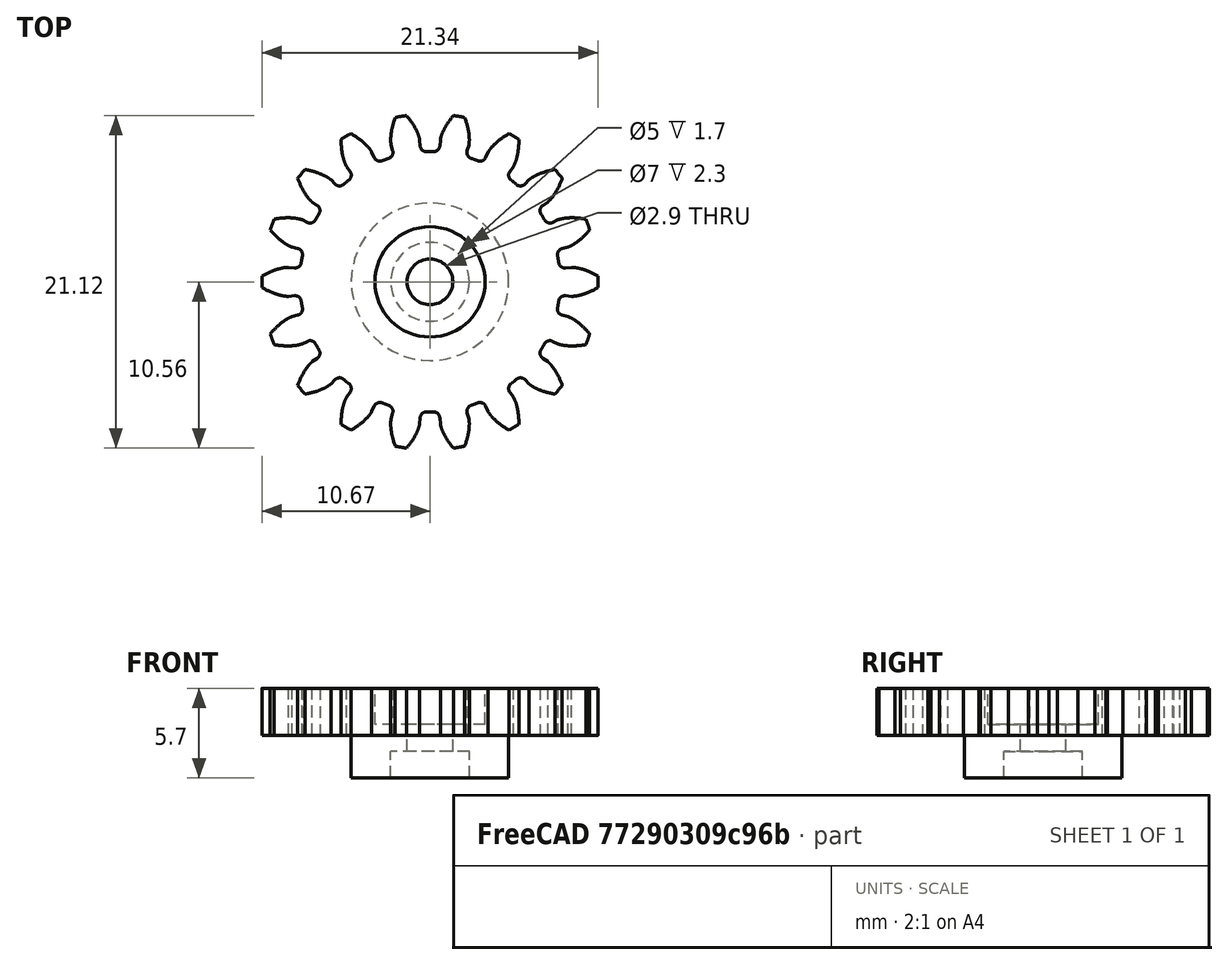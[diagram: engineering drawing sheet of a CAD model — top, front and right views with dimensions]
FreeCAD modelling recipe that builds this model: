
FCSTD DOCUMENT  (FreeCAD 0.17R13541 (Git))
Label: gear 18 low (new)
License: All rights reserved
LicenseURL: http://en.wikipedia.org/wiki/All_rights_reserved
objects: Part::Cylinder×5, Part::Cut×4, Part::Part2DObjectPython×1, Part::Extrusion×1, Part::MultiFuse×1
note: 12 computed .brp shape members not serialized (recipe doc carries the construction recipe); baked Part::Feature solids carry a one-line shape summary decoded from their .brp

FEATURE [Part::Part2DObjectPython] InvoluteGear  label="Engranaje 1 raw"  # Draft 2D object (typed FeaturePython)
  ExternalGear = true
  HighPrecision = true
  Modules = 1.0667
  NumberOfTeeth = 18
  PressureAngle = 20
  expr: Modules = 1.0667
FEATURE [Part::Extrusion] Extrude  label="Engranaje 1"
  Base = -> InvoluteGear
  Dir = (0,0,1)
  DirMode = 2
  FaceMakerClass = Part::FaceMakerBullseye
  LengthFwd = 3
  LengthRev = 0
  Solid = true
  Symmetric = false
FEATURE [Part::Cylinder] Cylinder  label="Cilindro"
  Angle = 360
  AttacherType = Attacher::AttachEngine3D
  Height = 10
  Placement = pos=(0,0,-2) rot=(0,0,1;0rad)
  Radius = 1.45
FEATURE [Part::Cut] Cut  label="Engranaje 1 agujereado"
  Base = -> Extrude
  Refine = true
  Tool = -> Cylinder
FEATURE [Part::Cylinder] Cylinder001  label="Cilindro exterior"
  Angle = 360
  AttacherType = Attacher::AttachEngine3D
  Height = 2.7
  Placement = pos=(0,0,-2.7) rot=(0,0,1;0rad)
  Radius = 5
FEATURE [Part::Cylinder] Cylinder002  label="Cilindro interior"
  Angle = 360
  AttacherType = Attacher::AttachEngine3D
  Height = 2.7
  Placement = pos=(0,0,-3.7) rot=(0,0,1;0rad)
  Radius = 2.5
FEATURE [Part::Cut] Cut001  label="Cilindro inferior"
  Base = -> Cylinder001
  Refine = true
  Tool = -> Cylinder002
FEATURE [Part::Cylinder] Cylinder003  label="Cilindro superior"
  Angle = 360
  AttacherType = Attacher::AttachEngine3D
  Height = 2.3
  Placement = pos=(0,0,0.7) rot=(0,0,1;0rad)
  Radius = 3.5
FEATURE [Part::Cut] Cut002
  Base = -> Cut
  Refine = true
  Tool = -> Cylinder003
FEATURE [Part::MultiFuse] Fusion  label="Engranaje 1 previo"
  Refine = true
  Shapes = -> [Cut001,Cut002]
FEATURE [Part::Cylinder] Cylinder004  label="Cilindro adicional"
  Angle = 360
  AttacherType = Attacher::AttachEngine3D
  Height = 10
  Placement = pos=(0,0,-2) rot=(0,0,1;0rad)
  Radius = 1.45
FEATURE [Part::Cut] Cut003  label="Engranaje 1 final"
  Base = -> Fusion
  Refine = true
  Tool = -> Cylinder004
